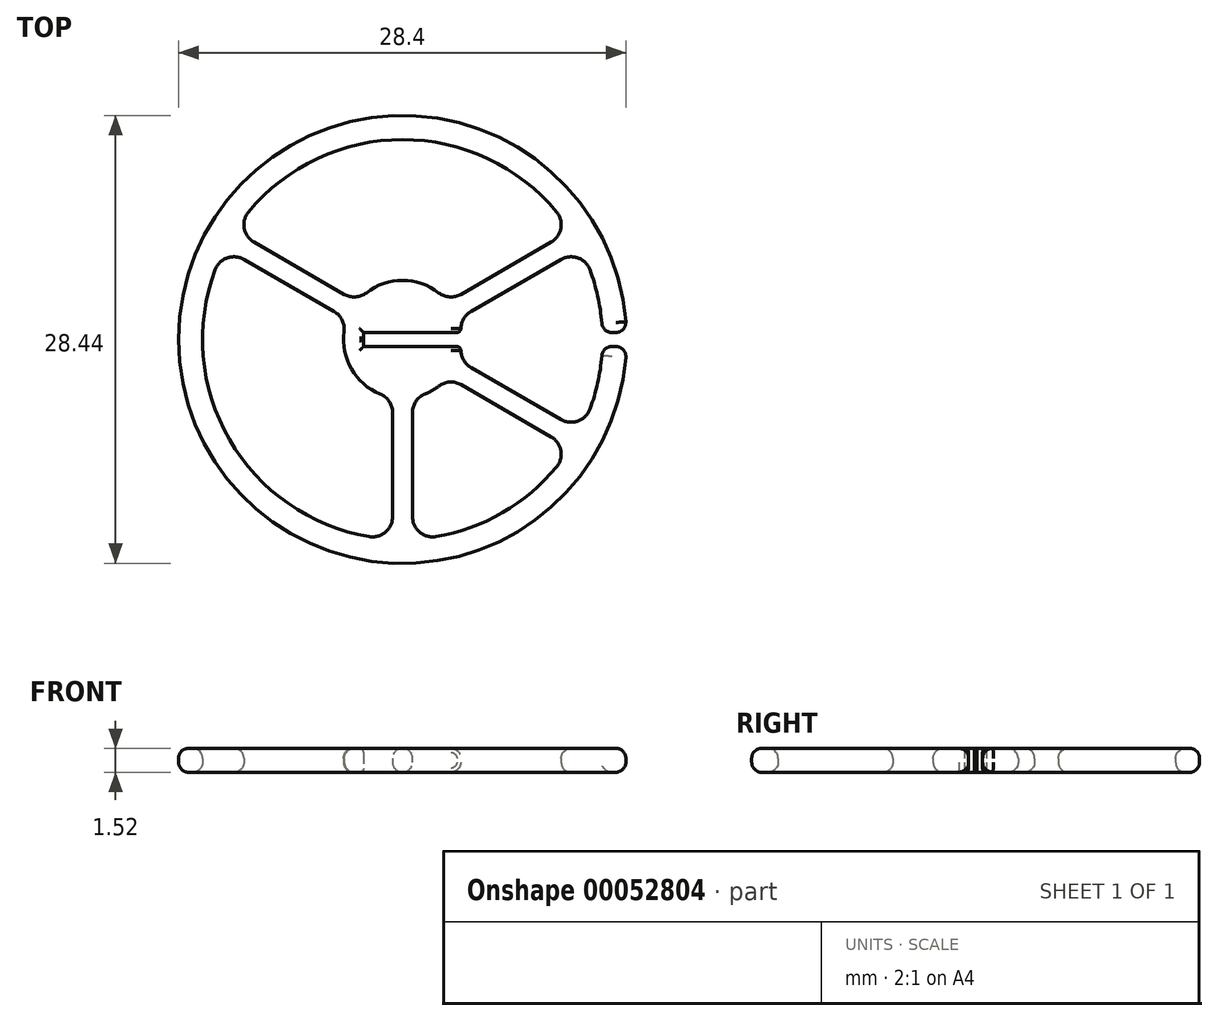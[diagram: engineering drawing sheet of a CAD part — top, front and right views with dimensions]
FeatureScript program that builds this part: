
annotation { "Feature Type Name" : "Feature", "Feature Type Description" : "" }
export const myFeature = defineFeature(function(context is Context, id is Id, definition is map)
    precondition{}
    {
        {
            var Q0;
            Q0=qCreatedBy(makeId("Top.planeOp"),FACE);
            var sketch = newSketch(context, id + "F0", { "sketchPlane" : qUnion([Q0])});
            skCircle(sketch, "E0", {"center": v(0, 0) * mm, "radius": 12.7 * mm});
            skLineSegment(sketch, "E1", {"start": v(0, 0) * mm, "end": v(11, 6.35) * mm});
            skLineSegment(sketch, "E2", {"start": v(0, 0) * mm, "end": v(0, -12.7) * mm});
            skLineSegment(sketch, "E3", {"start": v(0, 0) * mm, "end": v(-11, 6.35) * mm});
            skCircle(sketch, "E4", {"center": v(0, 0) * mm, "radius": 14.22 * mm});
            skLineSegment(sketch, "E5", {"start": v(-0.63, -12.68) * mm, "end": v(-0.64, -0.37) * mm});
            skLineSegment(sketch, "E6", {"start": v(0.63, -0.37) * mm, "end": v(0.64, -12.68) * mm});
            skLineSegment(sketch, "E7", {"start": v(0.64, -12.68) * mm, "end": v(-0.63, -12.68) * mm});
            skLineSegment(sketch, "E8", {"start": v(-11.3, 5.8) * mm, "end": v(-0.63, -0.37) * mm});
            skLineSegment(sketch, "E9", {"start": v(-0.63, -0.37) * mm, "end": v(0, 0.73) * mm});
            skLineSegment(sketch, "E10", {"start": v(0, 0.73) * mm, "end": v(-10.67, 6.9) * mm});
            skLineSegment(sketch, "E11", {"start": v(-10.67, 6.9) * mm, "end": v(-11.3, 5.8) * mm});
            skLineSegment(sketch, "E12", {"start": v(10.67, 6.9) * mm, "end": v(0, 0.73) * mm});
            skLineSegment(sketch, "E13", {"start": v(0, 0.73) * mm, "end": v(0.64, -0.37) * mm});
            skLineSegment(sketch, "E14", {"start": v(0.64, -0.37) * mm, "end": v(11.3, 5.8) * mm});
            skLineSegment(sketch, "E15", {"start": v(11.3, 5.8) * mm, "end": v(10.67, 6.9) * mm});
            skLineSegment(sketch, "E16", {"start": v(0.64, -0.37) * mm, "end": v(-0.63, -0.37) * mm});
            skCircle(sketch, "E17", {"center": v(0, 0) * mm, "radius": 3.75 * mm});
            skCircle(sketch, "E18", {"center": v(0, 0) * mm, "radius": 2.48 * mm});
            skLineSegment(sketch, "E19.bottom", {"start": v(14.9, -0.44) * mm, "end": v(-2.48, -0.44) * mm});
            skLineSegment(sketch, "E19.top", {"start": v(14.9, 0.44) * mm, "end": v(-2.48, 0.44) * mm});
            skLineSegment(sketch, "E19.left", {"start": v(14.9, -0.44) * mm, "end": v(14.9, 0.44) * mm});
            skLineSegment(sketch, "E19.right", {"start": v(-2.48, -0.44) * mm, "end": v(-2.48, 0.44) * mm});
            skLineSegment(sketch, "E20", {"start": v(10.67, -6.9) * mm, "end": v(0.14, -0.81) * mm});
            skLineSegment(sketch, "E21", {"start": v(0.14, -0.81) * mm, "end": v(0.77, 0.29) * mm});
            skLineSegment(sketch, "E22", {"start": v(0.77, 0.29) * mm, "end": v(11.3, -5.8) * mm});
            skLineSegment(sketch, "E23", {"start": v(11.3, -5.8) * mm, "end": v(10.67, -6.9) * mm});
            skLineSegment(sketch, "E24", {"start": v(0, 0) * mm, "end": v(11, -6.35) * mm});
            skSolve(sketch);
        }
        {
            var Q0;
            {var subQ0=sQuery(id+"F0.wireOp",EDGE,"E17");var subQ1=sQuery(id+"F0.wireOp",EDGE,"E3");var subQ2=makeQuery(id+"F0.imprint","INTERSECT",VERTEX,{"derivedFrom":[subQ1,subQ0]});Q0=makeQuery(id+"F0.imprint","IMPRINT",FACE,{"disambiguationData":[TD([[makeQuery(id+"F0.imprint","IMPRINT",EDGE,{"disambiguationData":[TD([[subQ2,-1.0]])],"derivedFrom":subQ1}),1.0]])]});}
            var Q1;
            {var subQ0=sQuery(id+"F0.wireOp",EDGE,"E17");var subQ1=sQuery(id+"F0.wireOp",EDGE,"E3");var subQ2=makeQuery(id+"F0.imprint","INTERSECT",VERTEX,{"derivedFrom":[subQ1,subQ0]});Q1=makeQuery(id+"F0.imprint","IMPRINT",FACE,{"disambiguationData":[TD([[makeQuery(id+"F0.imprint","IMPRINT",EDGE,{"disambiguationData":[TD([[subQ2,-1.0]])],"derivedFrom":subQ1}),-1.0]])]});}
            var Q2;
            {var subQ0=sQuery(id+"F0.wireOp",EDGE,"E18");var subQ1=sQuery(id+"F0.wireOp",EDGE,"E3");var subQ2=makeQuery(id+"F0.imprint","INTERSECT",VERTEX,{"derivedFrom":[subQ1,subQ0]});Q2=makeQuery(id+"F0.imprint","IMPRINT",FACE,{"disambiguationData":[TD([[makeQuery(id+"F0.imprint","IMPRINT",EDGE,{"disambiguationData":[TD([[subQ2,-1.0]])],"derivedFrom":subQ1}),1.0]])]});}
            var Q3;
            {var subQ0=sQuery(id+"F0.wireOp",EDGE,"E18");var subQ1=sQuery(id+"F0.wireOp",EDGE,"E3");var subQ2=makeQuery(id+"F0.imprint","INTERSECT",VERTEX,{"derivedFrom":[subQ1,subQ0]});Q3=makeQuery(id+"F0.imprint","IMPRINT",FACE,{"disambiguationData":[TD([[makeQuery(id+"F0.imprint","IMPRINT",EDGE,{"disambiguationData":[TD([[subQ2,-1.0]])],"derivedFrom":subQ1}),-1.0]])]});}
            var Q4;
            {var subQ0=sQuery(id+"F0.wireOp",EDGE,"E18");var subQ1=sQuery(id+"F0.wireOp",EDGE,"E10");var subQ2=makeQuery(id+"F0.imprint","INTERSECT",VERTEX,{"derivedFrom":[subQ1,subQ0]});Q4=makeQuery(id+"F0.imprint","IMPRINT",FACE,{"disambiguationData":[TD([[makeQuery(id+"F0.imprint","IMPRINT",EDGE,{"disambiguationData":[TD([[subQ2,-1.0]])],"derivedFrom":subQ1}),-1.0]])]});}
            var Q5;
            {var subQ0=sQuery(id+"F0.wireOp",EDGE,"E17");var subQ1=sQuery(id+"F0.wireOp",EDGE,"E5");var subQ2=makeQuery(id+"F0.imprint","INTERSECT",VERTEX,{"derivedFrom":[subQ1,subQ0]});Q5=makeQuery(id+"F0.imprint","IMPRINT",FACE,{"disambiguationData":[TD([[makeQuery(id+"F0.imprint","IMPRINT",EDGE,{"disambiguationData":[TD([[subQ2,-1.0]])],"derivedFrom":subQ1}),1.0]])]});}
            var Q6;
            {var subQ0=sQuery(id+"F0.wireOp",EDGE,"E18");var subQ1=sQuery(id+"F0.wireOp",EDGE,"E2");var subQ2=makeQuery(id+"F0.imprint","INTERSECT",VERTEX,{"derivedFrom":[subQ1,subQ0]});Q6=makeQuery(id+"F0.imprint","IMPRINT",FACE,{"disambiguationData":[TD([[makeQuery(id+"F0.imprint","IMPRINT",EDGE,{"disambiguationData":[TD([[subQ2,-1.0]])],"derivedFrom":subQ1}),-1.0]])]});}
            var Q7;
            {var subQ0=sQuery(id+"F0.wireOp",EDGE,"E18");var subQ1=sQuery(id+"F0.wireOp",EDGE,"E2");var subQ2=makeQuery(id+"F0.imprint","INTERSECT",VERTEX,{"derivedFrom":[subQ1,subQ0]});Q7=makeQuery(id+"F0.imprint","IMPRINT",FACE,{"disambiguationData":[TD([[makeQuery(id+"F0.imprint","IMPRINT",EDGE,{"disambiguationData":[TD([[subQ2,-1.0]])],"derivedFrom":subQ1}),1.0]])]});}
            var Q8;
            {var subQ0=sQuery(id+"F0.wireOp",EDGE,"E17");var subQ1=sQuery(id+"F0.wireOp",EDGE,"E2");var subQ2=makeQuery(id+"F0.imprint","INTERSECT",VERTEX,{"derivedFrom":[subQ1,subQ0]});Q8=makeQuery(id+"F0.imprint","IMPRINT",FACE,{"disambiguationData":[TD([[makeQuery(id+"F0.imprint","IMPRINT",EDGE,{"disambiguationData":[TD([[subQ2,-1.0]])],"derivedFrom":subQ1}),-1.0]])]});}
            var Q9;
            {var subQ0=sQuery(id+"F0.wireOp",EDGE,"E17");var subQ1=sQuery(id+"F0.wireOp",EDGE,"E2");var subQ2=makeQuery(id+"F0.imprint","INTERSECT",VERTEX,{"derivedFrom":[subQ1,subQ0]});Q9=makeQuery(id+"F0.imprint","IMPRINT",FACE,{"disambiguationData":[TD([[makeQuery(id+"F0.imprint","IMPRINT",EDGE,{"disambiguationData":[TD([[subQ2,-1.0]])],"derivedFrom":subQ1}),1.0]])]});}
            var Q10;
            {var subQ0=sQuery(id+"F0.wireOp",EDGE,"E18");var subQ1=sQuery(id+"F0.wireOp",EDGE,"E6");var subQ2=makeQuery(id+"F0.imprint","INTERSECT",VERTEX,{"derivedFrom":[subQ1,subQ0]});Q10=makeQuery(id+"F0.imprint","IMPRINT",FACE,{"disambiguationData":[TD([[makeQuery(id+"F0.imprint","IMPRINT",EDGE,{"disambiguationData":[TD([[subQ2,-1.0]])],"derivedFrom":subQ1}),1.0]])]});}
            var Q11;
            {var subQ0=sQuery(id+"F0.wireOp",EDGE,"E18");var subQ1=sQuery(id+"F0.wireOp",EDGE,"E1");var subQ2=makeQuery(id+"F0.imprint","INTERSECT",VERTEX,{"derivedFrom":[subQ1,subQ0]});Q11=makeQuery(id+"F0.imprint","IMPRINT",FACE,{"disambiguationData":[TD([[makeQuery(id+"F0.imprint","IMPRINT",EDGE,{"disambiguationData":[TD([[subQ2,-1.0]])],"derivedFrom":subQ1}),-1.0]])]});}
            var Q12;
            {var subQ0=sQuery(id+"F0.wireOp",EDGE,"E18");var subQ1=sQuery(id+"F0.wireOp",EDGE,"E1");var subQ2=makeQuery(id+"F0.imprint","INTERSECT",VERTEX,{"derivedFrom":[subQ1,subQ0]});Q12=makeQuery(id+"F0.imprint","IMPRINT",FACE,{"disambiguationData":[TD([[makeQuery(id+"F0.imprint","IMPRINT",EDGE,{"disambiguationData":[TD([[subQ2,-1.0]])],"derivedFrom":subQ1}),1.0]])]});}
            var Q13;
            {var subQ0=sQuery(id+"F0.wireOp",EDGE,"E17");var subQ1=sQuery(id+"F0.wireOp",EDGE,"E1");var subQ2=makeQuery(id+"F0.imprint","INTERSECT",VERTEX,{"derivedFrom":[subQ1,subQ0]});Q13=makeQuery(id+"F0.imprint","IMPRINT",FACE,{"disambiguationData":[TD([[makeQuery(id+"F0.imprint","IMPRINT",EDGE,{"disambiguationData":[TD([[subQ2,-1.0]])],"derivedFrom":subQ1}),-1.0]])]});}
            var Q14;
            {var subQ0=sQuery(id+"F0.wireOp",EDGE,"E17");var subQ1=sQuery(id+"F0.wireOp",EDGE,"E1");var subQ2=makeQuery(id+"F0.imprint","INTERSECT",VERTEX,{"derivedFrom":[subQ1,subQ0]});Q14=makeQuery(id+"F0.imprint","IMPRINT",FACE,{"disambiguationData":[TD([[makeQuery(id+"F0.imprint","IMPRINT",EDGE,{"disambiguationData":[TD([[subQ2,-1.0]])],"derivedFrom":subQ1}),1.0]])]});}
            var Q15;
            {var subQ0=sQuery(id+"F0.wireOp",EDGE,"E3");var subQ1=sQuery(id+"F0.wireOp",EDGE,"E0");var subQ2=makeQuery(id+"F0.imprint","INTERSECT",VERTEX,{"derivedFrom":[subQ1,subQ0]});Q15=makeQuery(id+"F0.imprint","IMPRINT",FACE,{"disambiguationData":[TD([[makeQuery(id+"F0.imprint","IMPRINT",EDGE,{"disambiguationData":[TD([[subQ2,1.0]])],"derivedFrom":subQ0}),1.0]])]});}
            var Q16;
            {var subQ0=sQuery(id+"F0.wireOp",EDGE,"E3");var subQ1=sQuery(id+"F0.wireOp",EDGE,"E0");var subQ2=makeQuery(id+"F0.imprint","INTERSECT",VERTEX,{"derivedFrom":[subQ1,subQ0]});Q16=makeQuery(id+"F0.imprint","IMPRINT",FACE,{"disambiguationData":[TD([[makeQuery(id+"F0.imprint","IMPRINT",EDGE,{"disambiguationData":[TD([[subQ2,1.0]])],"derivedFrom":subQ0}),-1.0]])]});}
            var Q17;
            {var subQ0=sQuery(id+"F0.wireOp",EDGE,"E1");var subQ1=sQuery(id+"F0.wireOp",EDGE,"E0");var subQ2=makeQuery(id+"F0.imprint","INTERSECT",VERTEX,{"derivedFrom":[subQ1,subQ0]});Q17=makeQuery(id+"F0.imprint","IMPRINT",FACE,{"disambiguationData":[TD([[makeQuery(id+"F0.imprint","IMPRINT",EDGE,{"disambiguationData":[TD([[subQ2,1.0]])],"derivedFrom":subQ0}),1.0]])]});}
            var Q18;
            {var subQ0=sQuery(id+"F0.wireOp",EDGE,"E1");var subQ1=sQuery(id+"F0.wireOp",EDGE,"E0");var subQ2=makeQuery(id+"F0.imprint","INTERSECT",VERTEX,{"derivedFrom":[subQ1,subQ0]});Q18=makeQuery(id+"F0.imprint","IMPRINT",FACE,{"disambiguationData":[TD([[makeQuery(id+"F0.imprint","IMPRINT",EDGE,{"disambiguationData":[TD([[subQ2,1.0]])],"derivedFrom":subQ0}),-1.0]])]});}
            var Q19;
            {var subQ0=sQuery(id+"F0.wireOp",EDGE,"E2");var subQ1=sQuery(id+"F0.wireOp",EDGE,"E0");var subQ2=makeQuery(id+"F0.imprint","INTERSECT",VERTEX,{"derivedFrom":[subQ1,subQ0]});Q19=makeQuery(id+"F0.imprint","IMPRINT",FACE,{"disambiguationData":[TD([[makeQuery(id+"F0.imprint","IMPRINT",EDGE,{"disambiguationData":[TD([[subQ2,1.0]])],"derivedFrom":subQ0}),-1.0]])]});}
            var Q20;
            {var subQ0=sQuery(id+"F0.wireOp",EDGE,"E2");var subQ1=sQuery(id+"F0.wireOp",EDGE,"E0");var subQ2=makeQuery(id+"F0.imprint","INTERSECT",VERTEX,{"derivedFrom":[subQ1,subQ0]});Q20=makeQuery(id+"F0.imprint","IMPRINT",FACE,{"disambiguationData":[TD([[makeQuery(id+"F0.imprint","IMPRINT",EDGE,{"disambiguationData":[TD([[subQ2,1.0]])],"derivedFrom":subQ0}),1.0]])]});}
            var Q21;
            {var subQ0=sQuery(id+"F0.wireOp",EDGE,"E18");var subQ1=sQuery(id+"F0.wireOp",EDGE,"E14");var subQ2=makeQuery(id+"F0.imprint","INTERSECT",VERTEX,{"derivedFrom":[subQ1,subQ0]});Q21=makeQuery(id+"F0.imprint","IMPRINT",FACE,{"disambiguationData":[TD([[makeQuery(id+"F0.imprint","IMPRINT",EDGE,{"disambiguationData":[TD([[subQ2,-1.0]])],"derivedFrom":subQ1}),-1.0]])]});}
            var Q22;
            {var subQ0=sQuery(id+"F0.wireOp",EDGE,"E18");var subQ1=sQuery(id+"F0.wireOp",EDGE,"E5");var subQ2=makeQuery(id+"F0.imprint","INTERSECT",VERTEX,{"derivedFrom":[subQ1,subQ0]});Q22=makeQuery(id+"F0.imprint","IMPRINT",FACE,{"disambiguationData":[TD([[makeQuery(id+"F0.imprint","IMPRINT",EDGE,{"disambiguationData":[TD([[subQ2,-1.0]])],"derivedFrom":subQ1}),1.0]])]});}
            var Q23;
            {var subQ0=sQuery(id+"F0.wireOp",EDGE,"E18");var subQ1=sQuery(id+"F0.wireOp",EDGE,"E8");var subQ2=makeQuery(id+"F0.imprint","INTERSECT",VERTEX,{"derivedFrom":[subQ1,subQ0]});Q23=makeQuery(id+"F0.imprint","IMPRINT",FACE,{"disambiguationData":[TD([[makeQuery(id+"F0.imprint","IMPRINT",EDGE,{"disambiguationData":[TD([[subQ2,-1.0]])],"derivedFrom":subQ1}),-1.0]])]});}
            var Q24;
            {var subQ0=sQuery(id+"F0.wireOp",EDGE,"E19.top");var subQ1=sQuery(id+"F0.wireOp",EDGE,"E3");var subQ2=makeQuery(id+"F0.imprint","INTERSECT",VERTEX,{"derivedFrom":[subQ1,subQ0]});Q24=makeQuery(id+"F0.imprint","IMPRINT",FACE,{"disambiguationData":[TD([[makeQuery(id+"F0.imprint","IMPRINT",EDGE,{"disambiguationData":[TD([[subQ2,-1.0]])],"derivedFrom":subQ1}),1.0]])]});}
            var Q25;
            {var subQ1=sQuery(id+"F0.wireOp",EDGE,"E3");var subQ7=sQuery(id+"F0.wireOp",EDGE,"E19.top");var subQ9=makeQuery(id+"F0.imprint","INTERSECT",VERTEX,{"derivedFrom":[subQ1,subQ7]});Q25=makeQuery(id+"F0.imprint","IMPRINT",FACE,{"disambiguationData":[TD([[makeQuery(id+"F0.imprint","IMPRINT",EDGE,{"disambiguationData":[TD([[subQ9,-1.0]])],"derivedFrom":subQ1}),-1.0]])]});}
            var Q26;
            {var subQ1=sQuery(id+"F0.wireOp",EDGE,"E10");var subQ3=sQuery(id+"F0.wireOp",EDGE,"E18");var subQ4=makeQuery(id+"F0.imprint","INTERSECT",VERTEX,{"derivedFrom":[subQ1,subQ3]});Q26=makeQuery(id+"F0.imprint","IMPRINT",FACE,{"disambiguationData":[TD([[makeQuery(id+"F0.imprint","IMPRINT",EDGE,{"disambiguationData":[TD([[subQ4,1.0]])],"derivedFrom":subQ3}),1.0]])]});}
            var Q27;
            {var subQ1=sQuery(id+"F0.wireOp",EDGE,"E1");var subQ7=sQuery(id+"F0.wireOp",EDGE,"E19.top");var subQ9=makeQuery(id+"F0.imprint","INTERSECT",VERTEX,{"derivedFrom":[subQ1,subQ7]});Q27=makeQuery(id+"F0.imprint","IMPRINT",FACE,{"disambiguationData":[TD([[makeQuery(id+"F0.imprint","IMPRINT",EDGE,{"disambiguationData":[TD([[subQ9,-1.0]])],"derivedFrom":subQ1}),1.0]])]});}
            var Q28;
            {var subQ1=sQuery(id+"F0.wireOp",EDGE,"E9");var subQ3=sQuery(id+"F0.wireOp",EDGE,"E19.top");var subQ4=makeQuery(id+"F0.imprint","INTERSECT",VERTEX,{"derivedFrom":[subQ1,subQ3]});Q28=makeQuery(id+"F0.imprint","IMPRINT",FACE,{"disambiguationData":[TD([[makeQuery(id+"F0.imprint","IMPRINT",EDGE,{"disambiguationData":[TD([[subQ4,1.0]])],"derivedFrom":subQ3}),-1.0]])]});}
            var Q29;
            {var subQ0=sQuery(id+"F0.wireOp",EDGE,"E19.top");var subQ1=sQuery(id+"F0.wireOp",EDGE,"E1");var subQ2=makeQuery(id+"F0.imprint","INTERSECT",VERTEX,{"derivedFrom":[subQ1,subQ0]});Q29=makeQuery(id+"F0.imprint","IMPRINT",FACE,{"disambiguationData":[TD([[makeQuery(id+"F0.imprint","IMPRINT",EDGE,{"disambiguationData":[TD([[subQ2,-1.0]])],"derivedFrom":subQ1}),-1.0]])]});}
            var Q30;
            {var subQ0=sQuery(id+"F0.wireOp",EDGE,"E19.top");var subQ1=sQuery(id+"F0.wireOp",EDGE,"E14");var subQ2=makeQuery(id+"F0.imprint","INTERSECT",VERTEX,{"derivedFrom":[subQ1,subQ0]});Q30=makeQuery(id+"F0.imprint","IMPRINT",FACE,{"disambiguationData":[TD([[makeQuery(id+"F0.imprint","IMPRINT",EDGE,{"disambiguationData":[TD([[subQ2,-1.0]])],"derivedFrom":subQ1}),-1.0]])]});}
            var Q31;
            {var subQ0=sQuery(id+"F0.wireOp",EDGE,"E19.bottom");var subQ1=sQuery(id+"F0.wireOp",EDGE,"E6");var subQ2=makeQuery(id+"F0.imprint","INTERSECT",VERTEX,{"derivedFrom":[subQ1,subQ0]});Q31=makeQuery(id+"F0.imprint","IMPRINT",FACE,{"disambiguationData":[TD([[makeQuery(id+"F0.imprint","IMPRINT",EDGE,{"disambiguationData":[TD([[subQ2,-1.0]])],"derivedFrom":subQ1}),1.0]])]});}
            var Q32;
            {var subQ0=sQuery(id+"F0.wireOp",EDGE,"E19.bottom");var subQ1=sQuery(id+"F0.wireOp",EDGE,"E2");var subQ2=makeQuery(id+"F0.imprint","INTERSECT",VERTEX,{"derivedFrom":[subQ1,subQ0]});Q32=makeQuery(id+"F0.imprint","IMPRINT",FACE,{"disambiguationData":[TD([[makeQuery(id+"F0.imprint","IMPRINT",EDGE,{"disambiguationData":[TD([[subQ2,-1.0]])],"derivedFrom":subQ1}),1.0]])]});}
            var Q33;
            {var subQ0=sQuery(id+"F0.wireOp",EDGE,"E19.bottom");var subQ1=sQuery(id+"F0.wireOp",EDGE,"E2");var subQ2=makeQuery(id+"F0.imprint","INTERSECT",VERTEX,{"derivedFrom":[subQ1,subQ0]});Q33=makeQuery(id+"F0.imprint","IMPRINT",FACE,{"disambiguationData":[TD([[makeQuery(id+"F0.imprint","IMPRINT",EDGE,{"disambiguationData":[TD([[subQ2,-1.0]])],"derivedFrom":subQ1}),-1.0]])]});}
            var Q34;
            {var subQ0=sQuery(id+"F0.wireOp",EDGE,"E19.bottom");var subQ1=sQuery(id+"F0.wireOp",EDGE,"E6");var subQ2=makeQuery(id+"F0.imprint","INTERSECT",VERTEX,{"derivedFrom":[subQ1,subQ0]});Q34=makeQuery(id+"F0.imprint","IMPRINT",FACE,{"disambiguationData":[TD([[makeQuery(id+"F0.imprint","IMPRINT",EDGE,{"disambiguationData":[TD([[subQ2,-1.0]])],"derivedFrom":subQ1}),-1.0]])]});}
            var Q35;
            {var subQ0=sQuery(id+"F0.wireOp",EDGE,"E24");var subQ1=sQuery(id+"F0.wireOp",EDGE,"E18");var subQ2=makeQuery(id+"F0.imprint","INTERSECT",VERTEX,{"derivedFrom":[subQ1,subQ0]});Q35=makeQuery(id+"F0.imprint","IMPRINT",FACE,{"disambiguationData":[TD([[makeQuery(id+"F0.imprint","IMPRINT",EDGE,{"disambiguationData":[TD([[subQ2,-1.0]])],"derivedFrom":subQ1}),1.0]])]});}
            var Q36;
            {var subQ0=sQuery(id+"F0.wireOp",EDGE,"E20");var subQ1=sQuery(id+"F0.wireOp",EDGE,"E6");var subQ2=makeQuery(id+"F0.imprint","INTERSECT",VERTEX,{"derivedFrom":[subQ1,subQ0]});Q36=makeQuery(id+"F0.imprint","IMPRINT",FACE,{"disambiguationData":[TD([[makeQuery(id+"F0.imprint","IMPRINT",EDGE,{"disambiguationData":[TD([[subQ2,-1.0]])],"derivedFrom":subQ1}),1.0]])]});}
            var Q37;
            {var subQ0=sQuery(id+"F0.wireOp",EDGE,"E20");var subQ1=sQuery(id+"F0.wireOp",EDGE,"E17");var subQ2=makeQuery(id+"F0.imprint","INTERSECT",VERTEX,{"derivedFrom":[subQ1,subQ0]});Q37=makeQuery(id+"F0.imprint","IMPRINT",FACE,{"disambiguationData":[TD([[makeQuery(id+"F0.imprint","IMPRINT",EDGE,{"disambiguationData":[TD([[subQ2,-1.0]])],"derivedFrom":subQ1}),1.0]])]});}
            var Q38;
            {var subQ0=sQuery(id+"F0.wireOp",EDGE,"E24");var subQ1=sQuery(id+"F0.wireOp",EDGE,"E17");var subQ2=makeQuery(id+"F0.imprint","INTERSECT",VERTEX,{"derivedFrom":[subQ1,subQ0]});Q38=makeQuery(id+"F0.imprint","IMPRINT",FACE,{"disambiguationData":[TD([[makeQuery(id+"F0.imprint","IMPRINT",EDGE,{"disambiguationData":[TD([[subQ2,-1.0]])],"derivedFrom":subQ1}),1.0]])]});}
            var Q39;
            {var subQ0=sQuery(id+"F0.wireOp",EDGE,"E22");var subQ1=sQuery(id+"F0.wireOp",EDGE,"E17");var subQ2=makeQuery(id+"F0.imprint","INTERSECT",VERTEX,{"derivedFrom":[subQ1,subQ0]});Q39=makeQuery(id+"F0.imprint","IMPRINT",FACE,{"disambiguationData":[TD([[makeQuery(id+"F0.imprint","IMPRINT",EDGE,{"disambiguationData":[TD([[subQ2,-1.0]])],"derivedFrom":subQ1}),1.0]])]});}
            var Q40;
            {var subQ0=sQuery(id+"F0.wireOp",EDGE,"E22");var subQ1=sQuery(id+"F0.wireOp",EDGE,"E18");var subQ2=makeQuery(id+"F0.imprint","INTERSECT",VERTEX,{"derivedFrom":[subQ1,subQ0]});Q40=makeQuery(id+"F0.imprint","IMPRINT",FACE,{"disambiguationData":[TD([[makeQuery(id+"F0.imprint","IMPRINT",EDGE,{"disambiguationData":[TD([[subQ2,-1.0]])],"derivedFrom":subQ1}),1.0]])]});}
            var Q41;
            {var subQ0=sQuery(id+"F0.wireOp",EDGE,"E20");var subQ1=sQuery(id+"F0.wireOp",EDGE,"E17");var subQ2=makeQuery(id+"F0.imprint","INTERSECT",VERTEX,{"derivedFrom":[subQ1,subQ0]});Q41=makeQuery(id+"F0.imprint","IMPRINT",FACE,{"disambiguationData":[TD([[makeQuery(id+"F0.imprint","IMPRINT",EDGE,{"disambiguationData":[TD([[subQ2,-1.0]])],"derivedFrom":subQ1}),-1.0]])]});}
            var Q42;
            {var subQ0=sQuery(id+"F0.wireOp",EDGE,"E24");var subQ1=sQuery(id+"F0.wireOp",EDGE,"E17");var subQ2=makeQuery(id+"F0.imprint","INTERSECT",VERTEX,{"derivedFrom":[subQ1,subQ0]});Q42=makeQuery(id+"F0.imprint","IMPRINT",FACE,{"disambiguationData":[TD([[makeQuery(id+"F0.imprint","IMPRINT",EDGE,{"disambiguationData":[TD([[subQ2,-1.0]])],"derivedFrom":subQ1}),-1.0]])]});}
            var Q43;
            {var subQ1=sQuery(id+"F0.wireOp",EDGE,"E0");var subQ3=sQuery(id+"F0.wireOp",EDGE,"E24");var subQ4=makeQuery(id+"F0.imprint","INTERSECT",VERTEX,{"derivedFrom":[subQ1,subQ3]});Q43=makeQuery(id+"F0.imprint","IMPRINT",FACE,{"disambiguationData":[TD([[makeQuery(id+"F0.imprint","IMPRINT",EDGE,{"disambiguationData":[TD([[subQ4,1.0]])],"derivedFrom":subQ3}),1.0]])]});}
            var Q44;
            {var subQ8=sQuery(id+"F0.wireOp",EDGE,"E19.bottom");var subQ9=sQuery(id+"F0.wireOp",EDGE,"E4");var subQ10=makeQuery(id+"F0.imprint","INTERSECT",VERTEX,{"derivedFrom":[subQ9,subQ8]});Q44=makeQuery(id+"F0.imprint","IMPRINT",FACE,{"disambiguationData":[TD([[makeQuery(id+"F0.imprint","IMPRINT",EDGE,{"disambiguationData":[TD([[subQ10,1.0]])],"derivedFrom":subQ9}),1.0]])]});}
            var Q45;
            {var subQ1=sQuery(id+"F0.wireOp",EDGE,"E0");var subQ3=sQuery(id+"F0.wireOp",EDGE,"E24");var subQ4=makeQuery(id+"F0.imprint","INTERSECT",VERTEX,{"derivedFrom":[subQ1,subQ3]});Q45=makeQuery(id+"F0.imprint","IMPRINT",FACE,{"disambiguationData":[TD([[makeQuery(id+"F0.imprint","IMPRINT",EDGE,{"disambiguationData":[TD([[subQ4,1.0]])],"derivedFrom":subQ3}),-1.0]])]});}
            extrude(context, id + "F1", {"entities" : qUnion([Q0, Q1, Q2, Q3, Q4, Q5, Q6, Q7, Q8, Q9, Q10, Q11, Q12, Q13, Q14, Q15, Q16, Q17, Q18, Q19, Q20, Q21, Q22, Q23, Q24, Q25, Q26, Q27, Q28, Q29, Q30, Q31, Q32, Q33, Q34, Q35, Q36, Q37, Q38, Q39, Q40, Q41, Q42, Q43, Q44, Q45]), "depth" : 1.52 * mm});
        }
        {
            var Q0;
            Q0=makeQuery(id+"F1.opExtrude","SWEPT_EDGE",EDGE,{"disambiguationData":[OSD([sQuery(id+"F0.wireOp",EDGE,"E0"),sQuery(id+"F0.wireOp",EDGE,"E8"),sQuery(id+"F0.wireOp",EDGE,"E11")])]});
            var Q1;
            Q1=makeQuery(id+"F1.opExtrude","SWEPT_EDGE",EDGE,{"disambiguationData":[OSD([sQuery(id+"F0.wireOp",EDGE,"E0"),sQuery(id+"F0.wireOp",EDGE,"E14"),sQuery(id+"F0.wireOp",EDGE,"E15")])]});
            var Q2;
            Q2=makeQuery(id+"F1.opExtrude","SWEPT_EDGE",EDGE,{"disambiguationData":[OSD([sQuery(id+"F0.wireOp",EDGE,"E5"),sQuery(id+"F0.wireOp",EDGE,"E17")])]});
            var Q3;
            Q3=makeQuery(id+"F1.opExtrude","SWEPT_EDGE",EDGE,{"disambiguationData":[OSD([sQuery(id+"F0.wireOp",EDGE,"E8"),sQuery(id+"F0.wireOp",EDGE,"E17")])]});
            var Q4;
            Q4=makeQuery(id+"F1.opExtrude","SWEPT_EDGE",EDGE,{"disambiguationData":[OSD([sQuery(id+"F0.wireOp",EDGE,"E0"),sQuery(id+"F0.wireOp",EDGE,"E12"),sQuery(id+"F0.wireOp",EDGE,"E15")])]});
            var Q5;
            Q5=makeQuery(id+"F1.opExtrude","SWEPT_EDGE",EDGE,{"disambiguationData":[OSD([sQuery(id+"F0.wireOp",EDGE,"E0"),sQuery(id+"F0.wireOp",EDGE,"E5"),sQuery(id+"F0.wireOp",EDGE,"E7")])]});
            var Q6;
            Q6=makeQuery(id+"F1.opExtrude","SWEPT_EDGE",EDGE,{"disambiguationData":[OSD([sQuery(id+"F0.wireOp",EDGE,"E10"),sQuery(id+"F0.wireOp",EDGE,"E17")])]});
            var Q7;
            Q7=makeQuery(id+"F1.opExtrude","SWEPT_EDGE",EDGE,{"disambiguationData":[OSD([sQuery(id+"F0.wireOp",EDGE,"E12"),sQuery(id+"F0.wireOp",EDGE,"E17")])]});
            var Q8;
            Q8=makeQuery(id+"F1.opExtrude","SWEPT_EDGE",EDGE,{"disambiguationData":[OSD([sQuery(id+"F0.wireOp",EDGE,"E0"),sQuery(id+"F0.wireOp",EDGE,"E10"),sQuery(id+"F0.wireOp",EDGE,"E11")])]});
            var Q9;
            Q9=makeQuery(id+"F1.opExtrude","SWEPT_EDGE",EDGE,{"disambiguationData":[OSD([sQuery(id+"F0.wireOp",EDGE,"E14"),sQuery(id+"F0.wireOp",EDGE,"E17")])]});
            var Q10;
            Q10=makeQuery(id+"F1.opExtrude","SWEPT_EDGE",EDGE,{"disambiguationData":[OSD([sQuery(id+"F0.wireOp",EDGE,"E6"),sQuery(id+"F0.wireOp",EDGE,"E17")])]});
            var Q11;
            Q11=makeQuery(id+"F1.opExtrude","SWEPT_EDGE",EDGE,{"disambiguationData":[OSD([sQuery(id+"F0.wireOp",EDGE,"E0"),sQuery(id+"F0.wireOp",EDGE,"E6"),sQuery(id+"F0.wireOp",EDGE,"E7")])]});
            var Q12;
            Q12=makeQuery(id+"F1.opExtrude","SWEPT_EDGE",EDGE,{"disambiguationData":[OSD([sQuery(id+"F0.wireOp",EDGE,"E0"),sQuery(id+"F0.wireOp",EDGE,"E20"),sQuery(id+"F0.wireOp",EDGE,"E23")])]});
            var Q13;
            Q13=makeQuery(id+"F1.opExtrude","SWEPT_EDGE",EDGE,{"disambiguationData":[OSD([sQuery(id+"F0.wireOp",EDGE,"E0"),sQuery(id+"F0.wireOp",EDGE,"E22"),sQuery(id+"F0.wireOp",EDGE,"E23")])]});
            var Q14;
            Q14=makeQuery(id+"F1.opExtrude","SWEPT_EDGE",EDGE,{"disambiguationData":[OSD([sQuery(id+"F0.wireOp",EDGE,"E17"),sQuery(id+"F0.wireOp",EDGE,"E22")])]});
            var Q15;
            Q15=makeQuery(id+"F1.opExtrude","SWEPT_EDGE",EDGE,{"disambiguationData":[OSD([sQuery(id+"F0.wireOp",EDGE,"E17"),sQuery(id+"F0.wireOp",EDGE,"E20")])]});
            fillet(context, id + "F2", {"entities" : qUnion([Q0, Q1, Q2, Q3, Q4, Q5, Q6, Q7, Q8, Q9, Q10, Q11, Q12, Q13, Q14, Q15]), "radius" : 1.27 * mm, "tangentPropagation" : true, "allowEdgeOverflow" : false});
        }
        {
            var Q0;
            Q0=makeQuery(id+"F1.opExtrude","CAP_EDGE",EDGE,{"disambiguationData":[OSD([sQuery(id+"F0.wireOp",EDGE,"E4")])],"isStart":false});
            var Q1;
            {var subQ0=sQuery(id+"F0.wireOp",EDGE,"E0");Q1=makeQuery(id+"F1.opExtrude","CAP_EDGE",EDGE,{"disambiguationData":[OSD([subQ0]),TDD([makeQuery(id+"F0.imprint","IMPRINT",EDGE,{"disambiguationData":[TD([[makeQuery(id+"F0.imprint","INTERSECT",VERTEX,{"derivedFrom":[subQ0,sQuery(id+"F0.wireOp",EDGE,"E5"),sQuery(id+"F0.wireOp",EDGE,"E7")]}),1.0]])],"derivedFrom":subQ0})])],"isStart":false});}
            var Q2;
            Q2=makeQuery(id+"F1.opExtrude","CAP_EDGE",EDGE,{"disambiguationData":[OSD([sQuery(id+"F0.wireOp",EDGE,"E6")])],"isStart":false});
            var Q3;
            Q3=makeQuery(id+"F1.opExtrude","CAP_EDGE",EDGE,{"disambiguationData":[OSD([sQuery(id+"F0.wireOp",EDGE,"E22")])],"isStart":false});
            var Q4;
            {var subQ0=sQuery(id+"F0.wireOp",EDGE,"E0");Q4=makeQuery(id+"F1.opExtrude","CAP_EDGE",EDGE,{"disambiguationData":[OSD([subQ0]),TDD([makeQuery(id+"F0.imprint","IMPRINT",EDGE,{"disambiguationData":[TD([[makeQuery(id+"F0.imprint","INTERSECT",VERTEX,{"derivedFrom":[subQ0,sQuery(id+"F0.wireOp",EDGE,"E19.top")]}),-1.0]])],"derivedFrom":subQ0})])],"isStart":false});}
            var Q5;
            {var subQ0=sQuery(id+"F0.wireOp",EDGE,"E0");Q5=makeQuery(id+"F1.opExtrude","CAP_EDGE",EDGE,{"disambiguationData":[OSD([subQ0]),TDD([makeQuery(id+"F0.imprint","IMPRINT",EDGE,{"disambiguationData":[TD([[makeQuery(id+"F0.imprint","INTERSECT",VERTEX,{"derivedFrom":[subQ0,sQuery(id+"F0.wireOp",EDGE,"E10"),sQuery(id+"F0.wireOp",EDGE,"E11")]}),1.0]])],"derivedFrom":subQ0})])],"isStart":false});}
            var Q6;
            {var subQ0=sQuery(id+"F0.wireOp",EDGE,"E19.top");Q6=makeQuery(id+"F1.opExtrude","CAP_EDGE",EDGE,{"disambiguationData":[OSD([subQ0]),TDD([makeQuery(id+"F0.imprint","IMPRINT",EDGE,{"disambiguationData":[TD([[makeQuery(id+"F0.imprint","INTERSECT",VERTEX,{"derivedFrom":[sQuery(id+"F0.wireOp",EDGE,"E4"),subQ0]}),-1.0]])],"derivedFrom":subQ0})])],"isStart":false});}
            var Q7;
            Q7=makeQuery(id+"F1.opExtrude","CAP_EDGE",EDGE,{"disambiguationData":[OSD([sQuery(id+"F0.wireOp",EDGE,"E8")])],"isStart":true});
            var Q8;
            Q8=makeQuery(id+"F1.opExtrude","CAP_EDGE",EDGE,{"disambiguationData":[OSD([sQuery(id+"F0.wireOp",EDGE,"E10")])],"isStart":true});
            var Q9;
            Q9=makeQuery(id+"F1.opExtrude","CAP_EDGE",EDGE,{"disambiguationData":[OSD([sQuery(id+"F0.wireOp",EDGE,"E14")])],"isStart":true});
            var Q10;
            {var subQ0=sQuery(id+"F0.wireOp",EDGE,"E0");Q10=makeQuery(id+"F1.opExtrude","CAP_EDGE",EDGE,{"disambiguationData":[OSD([subQ0]),TDD([makeQuery(id+"F0.imprint","IMPRINT",EDGE,{"disambiguationData":[TD([[makeQuery(id+"F0.imprint","INTERSECT",VERTEX,{"derivedFrom":[subQ0,sQuery(id+"F0.wireOp",EDGE,"E19.bottom")]}),1.0]])],"derivedFrom":subQ0})])],"isStart":true});}
            var Q11;
            {var subQ0=sQuery(id+"F0.wireOp",EDGE,"E20");var subQ1=sQuery(id+"F0.wireOp",EDGE,"E17");Q11=makeQuery(id+"F2.opFillet","BLEND_EDGE",EDGE,{"blendedFrom":[makeQuery(id+"F1.opExtrude","SWEPT_EDGE",EDGE,{"disambiguationData":[OSD([subQ1,subQ0])]}),makeQuery(id+"F1.opExtrude","CAP_FACE",FACE,{"disambiguationData":[OSD([sQuery(id+"F0.wireOp",EDGE,"E0"),sQuery(id+"F0.wireOp",EDGE,"E4"),sQuery(id+"F0.wireOp",EDGE,"E5"),sQuery(id+"F0.wireOp",EDGE,"E6"),sQuery(id+"F0.wireOp",EDGE,"E8"),sQuery(id+"F0.wireOp",EDGE,"E10"),sQuery(id+"F0.wireOp",EDGE,"E12"),sQuery(id+"F0.wireOp",EDGE,"E14"),subQ1,sQuery(id+"F0.wireOp",EDGE,"E18"),sQuery(id+"F0.wireOp",EDGE,"E19.bottom"),sQuery(id+"F0.wireOp",EDGE,"E19.top"),sQuery(id+"F0.wireOp",EDGE,"E19.right"),subQ0,sQuery(id+"F0.wireOp",EDGE,"E22")])],"isStart":true})],"blendedInto":[makeQuery(id+"F1.opExtrude","CAP_FACE",FACE,{"disambiguationData":[OSD([sQuery(id+"F0.wireOp",EDGE,"E0"),sQuery(id+"F0.wireOp",EDGE,"E4"),sQuery(id+"F0.wireOp",EDGE,"E5"),sQuery(id+"F0.wireOp",EDGE,"E6"),sQuery(id+"F0.wireOp",EDGE,"E8"),sQuery(id+"F0.wireOp",EDGE,"E10"),sQuery(id+"F0.wireOp",EDGE,"E12"),sQuery(id+"F0.wireOp",EDGE,"E14"),subQ1,sQuery(id+"F0.wireOp",EDGE,"E18"),sQuery(id+"F0.wireOp",EDGE,"E19.bottom"),sQuery(id+"F0.wireOp",EDGE,"E19.top"),sQuery(id+"F0.wireOp",EDGE,"E19.right"),subQ0,sQuery(id+"F0.wireOp",EDGE,"E22")])],"isStart":true})]});}
            var Q12;
            Q12=makeQuery(id+"F1.opExtrude","SWEPT_EDGE",EDGE,{"disambiguationData":[OSD([sQuery(id+"F0.wireOp",EDGE,"E4"),sQuery(id+"F0.wireOp",EDGE,"E19.top")])]});
            var Q13;
            Q13=makeQuery(id+"F1.opExtrude","SWEPT_EDGE",EDGE,{"disambiguationData":[OSD([sQuery(id+"F0.wireOp",EDGE,"E4"),sQuery(id+"F0.wireOp",EDGE,"E19.bottom")])]});
            var Q14;
            {var subQ0=sQuery(id+"F0.wireOp",EDGE,"E19.bottom");Q14=makeQuery(id+"F1.opExtrude","CAP_EDGE",EDGE,{"disambiguationData":[OSD([subQ0]),TDD([makeQuery(id+"F0.imprint","IMPRINT",EDGE,{"disambiguationData":[TD([[makeQuery(id+"F0.imprint","INTERSECT",VERTEX,{"derivedFrom":[sQuery(id+"F0.wireOp",EDGE,"E4"),subQ0]}),-1.0]])],"derivedFrom":subQ0})])],"isStart":true});}
            var Q15;
            {var subQ0=sQuery(id+"F0.wireOp",EDGE,"E19.top");Q15=makeQuery(id+"F1.opExtrude","CAP_EDGE",EDGE,{"disambiguationData":[OSD([subQ0]),TDD([makeQuery(id+"F0.imprint","IMPRINT",EDGE,{"disambiguationData":[TD([[makeQuery(id+"F0.imprint","INTERSECT",VERTEX,{"derivedFrom":[sQuery(id+"F0.wireOp",EDGE,"E4"),subQ0]}),-1.0]])],"derivedFrom":subQ0})])],"isStart":true});}
            var Q16;
            Q16=makeQuery(id+"F1.opExtrude","SWEPT_EDGE",EDGE,{"disambiguationData":[OSD([sQuery(id+"F0.wireOp",EDGE,"E0"),sQuery(id+"F0.wireOp",EDGE,"E19.top")])]});
            var Q17;
            Q17=makeQuery(id+"F1.opExtrude","SWEPT_EDGE",EDGE,{"disambiguationData":[OSD([sQuery(id+"F0.wireOp",EDGE,"E0"),sQuery(id+"F0.wireOp",EDGE,"E19.bottom")])]});
            var Q18;
            {var subQ0=sQuery(id+"F0.wireOp",EDGE,"E19.bottom");Q18=makeQuery(id+"F1.opExtrude","CAP_EDGE",EDGE,{"disambiguationData":[OSD([subQ0]),TDD([makeQuery(id+"F0.imprint","IMPRINT",EDGE,{"disambiguationData":[TD([[makeQuery(id+"F0.imprint","INTERSECT",VERTEX,{"derivedFrom":[sQuery(id+"F0.wireOp",EDGE,"E4"),subQ0]}),-1.0]])],"derivedFrom":subQ0})])],"isStart":false});}
            var Q19;
            Q19=makeQuery(id+"F1.opExtrude","CAP_EDGE",EDGE,{"disambiguationData":[OSD([sQuery(id+"F0.wireOp",EDGE,"E4")])],"isStart":true});
            fillet(context, id + "F3", {"entities" : qUnion([Q0, Q1, Q2, Q3, Q4, Q5, Q6, Q7, Q8, Q9, Q10, Q11, Q12, Q13, Q14, Q15, Q16, Q17, Q18, Q19]), "radius" : 0.64 * mm, "tangentPropagation" : true, "allowEdgeOverflow" : false});
        }
        {
            var Q0;
            {var subQ0=sQuery(id+"F0.wireOp",EDGE,"E19.top");var subQ3=makeQuery(id+"F0.imprint","INTERSECT",VERTEX,{"derivedFrom":[sQuery(id+"F0.wireOp",EDGE,"E8"),subQ0]});var subQ4=makeQuery(id+"F0.imprint","INTERSECT",VERTEX,{"derivedFrom":[sQuery(id+"F0.wireOp",EDGE,"E3"),subQ0]});var subQ5=makeQuery(id+"F0.imprint","INTERSECT",VERTEX,{"derivedFrom":[sQuery(id+"F0.wireOp",EDGE,"E9"),subQ0]});var subQ7=makeQuery(id+"F0.imprint","INTERSECT",VERTEX,{"derivedFrom":[sQuery(id+"F0.wireOp",EDGE,"E1"),subQ0]});var subQ8=makeQuery(id+"F0.imprint","INTERSECT",VERTEX,{"derivedFrom":[sQuery(id+"F0.wireOp",EDGE,"E14"),subQ0]});Q0=makeQuery(id+"F1.opExtrude","CAP_EDGE",EDGE,{"disambiguationData":[OSD([subQ0]),TDD([makeQuery(id+"F0.imprint","IMPRINT",EDGE,{"disambiguationData":[TD([[makeQuery(id+"F0.imprint","INTERSECT",VERTEX,{"derivedFrom":[sQuery(id+"F0.wireOp",EDGE,"E17"),subQ0]}),-1.0]])],"derivedFrom":subQ0}),makeQuery(id+"F0.imprint","IMPRINT",EDGE,{"disambiguationData":[TD([[subQ8,1.0]])],"derivedFrom":subQ0}),makeQuery(id+"F0.imprint","IMPRINT",EDGE,{"disambiguationData":[TD([[subQ7,1.0]])],"derivedFrom":subQ0}),makeQuery(id+"F0.imprint","IMPRINT",EDGE,{"disambiguationData":[TD([[subQ7,-1.0]])],"derivedFrom":subQ0}),makeQuery(id+"F0.imprint","IMPRINT",EDGE,{"disambiguationData":[TD([[subQ5,1.0]])],"derivedFrom":subQ0}),makeQuery(id+"F0.imprint","IMPRINT",EDGE,{"disambiguationData":[TD([[subQ4,1.0]])],"derivedFrom":subQ0}),makeQuery(id+"F0.imprint","IMPRINT",EDGE,{"disambiguationData":[TD([[subQ4,-1.0]])],"derivedFrom":subQ0}),makeQuery(id+"F0.imprint","IMPRINT",EDGE,{"disambiguationData":[TD([[subQ3,-1.0]])],"derivedFrom":subQ0}),makeQuery(id+"F0.imprint","IMPRINT",EDGE,{"disambiguationData":[TD([[makeQuery(id+"F0.imprint","INTERSECT",VERTEX,{"derivedFrom":[subQ0,sQuery(id+"F0.wireOp",EDGE,"E19.right")]}),1.0]])],"derivedFrom":subQ0})])],"isStart":false});}
            var Q1;
            {var subQ0=sQuery(id+"F0.wireOp",EDGE,"E19.right");Q1=makeQuery(id+"F1.opExtrude","CAP_EDGE",EDGE,{"disambiguationData":[OSD([subQ0]),TDD([makeQuery(id+"F0.imprint","IMPRINT",EDGE,{"disambiguationData":[TD([[makeQuery(id+"F0.imprint","INTERSECT",VERTEX,{"derivedFrom":[sQuery(id+"F0.wireOp",EDGE,"E19.top"),subQ0]}),1.0]])],"derivedFrom":subQ0})])],"isStart":false});}
            var Q2;
            {var subQ0=sQuery(id+"F0.wireOp",EDGE,"E19.right");Q2=makeQuery(id+"F1.opExtrude","CAP_EDGE",EDGE,{"disambiguationData":[OSD([subQ0]),TDD([makeQuery(id+"F0.imprint","IMPRINT",EDGE,{"disambiguationData":[TD([[makeQuery(id+"F0.imprint","INTERSECT",VERTEX,{"derivedFrom":[sQuery(id+"F0.wireOp",EDGE,"E19.bottom"),subQ0]}),-1.0]])],"derivedFrom":subQ0})])],"isStart":false});}
            var Q3;
            Q3=makeQuery(id+"F1.opExtrude","CAP_EDGE",EDGE,{"disambiguationData":[OSD([sQuery(id+"F0.wireOp",EDGE,"E18")])],"isStart":false});
            var Q4;
            {var subQ0=sQuery(id+"F0.wireOp",EDGE,"E19.bottom");var subQ1=sQuery(id+"F0.wireOp",EDGE,"E18");var subQ3=makeQuery(id+"F0.imprint","INTERSECT",VERTEX,{"derivedFrom":[sQuery(id+"F0.wireOp",EDGE,"E5"),subQ0]});var subQ4=makeQuery(id+"F0.imprint","INTERSECT",VERTEX,{"derivedFrom":[sQuery(id+"F0.wireOp",EDGE,"E2"),subQ0]});var subQ6=makeQuery(id+"F0.imprint","INTERSECT",VERTEX,{"derivedFrom":[sQuery(id+"F0.wireOp",EDGE,"E6"),subQ0]});var subQ8=makeQuery(id+"F0.imprint","INTERSECT",VERTEX,{"derivedFrom":[subQ0,sQuery(id+"F0.wireOp",EDGE,"E22")]});var subQ9=makeQuery(id+"F0.imprint","INTERSECT",VERTEX,{"disambiguationData":[OD(1.0)],"derivedFrom":[subQ1,subQ0]});Q4=makeQuery(id+"F1.opExtrude","CAP_EDGE",EDGE,{"disambiguationData":[OSD([subQ0]),TDD([makeQuery(id+"F0.imprint","IMPRINT",EDGE,{"disambiguationData":[TD([[makeQuery(id+"F0.imprint","INTERSECT",VERTEX,{"derivedFrom":[sQuery(id+"F0.wireOp",EDGE,"E17"),subQ0]}),-1.0]])],"derivedFrom":subQ0}),makeQuery(id+"F0.imprint","IMPRINT",EDGE,{"disambiguationData":[TD([[subQ9,-1.0]])],"derivedFrom":subQ0}),makeQuery(id+"F0.imprint","IMPRINT",EDGE,{"disambiguationData":[TD([[subQ8,-1.0]])],"derivedFrom":subQ0}),makeQuery(id+"F0.imprint","IMPRINT",EDGE,{"disambiguationData":[TD([[subQ6,1.0]])],"derivedFrom":subQ0}),makeQuery(id+"F0.imprint","IMPRINT",EDGE,{"disambiguationData":[TD([[subQ6,-1.0]])],"derivedFrom":subQ0}),makeQuery(id+"F0.imprint","IMPRINT",EDGE,{"disambiguationData":[TD([[subQ4,1.0]])],"derivedFrom":subQ0}),makeQuery(id+"F0.imprint","IMPRINT",EDGE,{"disambiguationData":[TD([[subQ4,-1.0]])],"derivedFrom":subQ0}),makeQuery(id+"F0.imprint","IMPRINT",EDGE,{"disambiguationData":[TD([[subQ3,-1.0]])],"derivedFrom":subQ0}),makeQuery(id+"F0.imprint","IMPRINT",EDGE,{"disambiguationData":[TD([[makeQuery(id+"F0.imprint","INTERSECT",VERTEX,{"derivedFrom":[subQ0,sQuery(id+"F0.wireOp",EDGE,"E19.right")]}),1.0]])],"derivedFrom":subQ0})])],"isStart":false});}
            var Q5;
            {var subQ0=sQuery(id+"F0.wireOp",EDGE,"E19.right");var subQ1=sQuery(id+"F0.wireOp",EDGE,"E19.top");var subQ2=sQuery(id+"F0.wireOp",EDGE,"E18");var subQ4=sQuery(id+"F0.wireOp",EDGE,"E8");var subQ5=makeQuery(id+"F0.imprint","INTERSECT",VERTEX,{"derivedFrom":[subQ4,subQ1]});var subQ6=makeQuery(id+"F0.imprint","INTERSECT",VERTEX,{"derivedFrom":[sQuery(id+"F0.wireOp",EDGE,"E3"),subQ1]});var subQ7=makeQuery(id+"F0.imprint","INTERSECT",VERTEX,{"derivedFrom":[sQuery(id+"F0.wireOp",EDGE,"E9"),subQ1]});var subQ9=makeQuery(id+"F0.imprint","INTERSECT",VERTEX,{"derivedFrom":[sQuery(id+"F0.wireOp",EDGE,"E1"),subQ1]});var subQ10=sQuery(id+"F0.wireOp",EDGE,"E14");var subQ11=makeQuery(id+"F0.imprint","INTERSECT",VERTEX,{"derivedFrom":[subQ10,subQ1]});var subQ13=sQuery(id+"F0.wireOp",EDGE,"E17");Q5=makeQuery(id+"F3.opFillet","BLEND_EDGE",EDGE,{"blendedFrom":[makeQuery(id+"F2.opFillet","BLEND_EDGE",EDGE,{"blendedFrom":[makeQuery(id+"F1.opExtrude","SWEPT_EDGE",EDGE,{"disambiguationData":[OSD([subQ10,subQ13])]}),makeQuery(id+"F1.opExtrude","CAP_FACE",FACE,{"disambiguationData":[OSD([sQuery(id+"F0.wireOp",EDGE,"E0"),sQuery(id+"F0.wireOp",EDGE,"E4"),sQuery(id+"F0.wireOp",EDGE,"E5"),sQuery(id+"F0.wireOp",EDGE,"E6"),subQ4,sQuery(id+"F0.wireOp",EDGE,"E10"),sQuery(id+"F0.wireOp",EDGE,"E12"),subQ10,subQ13,subQ2,sQuery(id+"F0.wireOp",EDGE,"E19.bottom"),subQ1,subQ0,sQuery(id+"F0.wireOp",EDGE,"E20"),sQuery(id+"F0.wireOp",EDGE,"E22")])],"isStart":false})],"blendedInto":[makeQuery(id+"F1.opExtrude","CAP_FACE",FACE,{"disambiguationData":[OSD([sQuery(id+"F0.wireOp",EDGE,"E0"),sQuery(id+"F0.wireOp",EDGE,"E4"),sQuery(id+"F0.wireOp",EDGE,"E5"),sQuery(id+"F0.wireOp",EDGE,"E6"),subQ4,sQuery(id+"F0.wireOp",EDGE,"E10"),sQuery(id+"F0.wireOp",EDGE,"E12"),subQ10,subQ13,subQ2,sQuery(id+"F0.wireOp",EDGE,"E19.bottom"),subQ1,subQ0,sQuery(id+"F0.wireOp",EDGE,"E20"),sQuery(id+"F0.wireOp",EDGE,"E22")])],"isStart":false})]}),makeQuery(id+"F1.opExtrude","SWEPT_FACE",FACE,{"disambiguationData":[OSD([subQ1]),TDD([makeQuery(id+"F0.imprint","IMPRINT",EDGE,{"disambiguationData":[TD([[makeQuery(id+"F0.imprint","INTERSECT",VERTEX,{"derivedFrom":[subQ13,subQ1]}),-1.0]])],"derivedFrom":subQ1}),makeQuery(id+"F0.imprint","IMPRINT",EDGE,{"disambiguationData":[TD([[subQ11,1.0]])],"derivedFrom":subQ1}),makeQuery(id+"F0.imprint","IMPRINT",EDGE,{"disambiguationData":[TD([[subQ9,1.0]])],"derivedFrom":subQ1}),makeQuery(id+"F0.imprint","IMPRINT",EDGE,{"disambiguationData":[TD([[subQ9,-1.0]])],"derivedFrom":subQ1}),makeQuery(id+"F0.imprint","IMPRINT",EDGE,{"disambiguationData":[TD([[subQ7,1.0]])],"derivedFrom":subQ1}),makeQuery(id+"F0.imprint","IMPRINT",EDGE,{"disambiguationData":[TD([[subQ6,1.0]])],"derivedFrom":subQ1}),makeQuery(id+"F0.imprint","IMPRINT",EDGE,{"disambiguationData":[TD([[subQ6,-1.0]])],"derivedFrom":subQ1}),makeQuery(id+"F0.imprint","IMPRINT",EDGE,{"disambiguationData":[TD([[subQ5,-1.0]])],"derivedFrom":subQ1}),makeQuery(id+"F0.imprint","IMPRINT",EDGE,{"disambiguationData":[TD([[makeQuery(id+"F0.imprint","INTERSECT",VERTEX,{"derivedFrom":[subQ1,subQ0]}),1.0]])],"derivedFrom":subQ1})])]})],"blendedInto":[makeQuery(id+"F1.opExtrude","SWEPT_FACE",FACE,{"disambiguationData":[OSD([subQ1]),TDD([makeQuery(id+"F0.imprint","IMPRINT",EDGE,{"disambiguationData":[TD([[makeQuery(id+"F0.imprint","INTERSECT",VERTEX,{"derivedFrom":[subQ13,subQ1]}),-1.0]])],"derivedFrom":subQ1}),makeQuery(id+"F0.imprint","IMPRINT",EDGE,{"disambiguationData":[TD([[subQ11,1.0]])],"derivedFrom":subQ1}),makeQuery(id+"F0.imprint","IMPRINT",EDGE,{"disambiguationData":[TD([[subQ9,1.0]])],"derivedFrom":subQ1}),makeQuery(id+"F0.imprint","IMPRINT",EDGE,{"disambiguationData":[TD([[subQ9,-1.0]])],"derivedFrom":subQ1}),makeQuery(id+"F0.imprint","IMPRINT",EDGE,{"disambiguationData":[TD([[subQ7,1.0]])],"derivedFrom":subQ1}),makeQuery(id+"F0.imprint","IMPRINT",EDGE,{"disambiguationData":[TD([[subQ6,1.0]])],"derivedFrom":subQ1}),makeQuery(id+"F0.imprint","IMPRINT",EDGE,{"disambiguationData":[TD([[subQ6,-1.0]])],"derivedFrom":subQ1}),makeQuery(id+"F0.imprint","IMPRINT",EDGE,{"disambiguationData":[TD([[subQ5,-1.0]])],"derivedFrom":subQ1}),makeQuery(id+"F0.imprint","IMPRINT",EDGE,{"disambiguationData":[TD([[makeQuery(id+"F0.imprint","INTERSECT",VERTEX,{"derivedFrom":[subQ1,subQ0]}),1.0]])],"derivedFrom":subQ1})])]})]});}
            var Q6;
            {var subQ0=sQuery(id+"F0.wireOp",EDGE,"E19.right");var subQ1=sQuery(id+"F0.wireOp",EDGE,"E19.bottom");var subQ2=sQuery(id+"F0.wireOp",EDGE,"E18");var subQ4=sQuery(id+"F0.wireOp",EDGE,"E5");var subQ5=makeQuery(id+"F0.imprint","INTERSECT",VERTEX,{"derivedFrom":[subQ4,subQ1]});var subQ6=makeQuery(id+"F0.imprint","INTERSECT",VERTEX,{"derivedFrom":[sQuery(id+"F0.wireOp",EDGE,"E2"),subQ1]});var subQ8=sQuery(id+"F0.wireOp",EDGE,"E6");var subQ9=makeQuery(id+"F0.imprint","INTERSECT",VERTEX,{"derivedFrom":[subQ8,subQ1]});var subQ11=sQuery(id+"F0.wireOp",EDGE,"E22");var subQ12=makeQuery(id+"F0.imprint","INTERSECT",VERTEX,{"derivedFrom":[subQ1,subQ11]});var subQ13=makeQuery(id+"F0.imprint","INTERSECT",VERTEX,{"disambiguationData":[OD(1.0)],"derivedFrom":[subQ2,subQ1]});var subQ14=sQuery(id+"F0.wireOp",EDGE,"E17");Q6=makeQuery(id+"F3.opFillet","BLEND_EDGE",EDGE,{"blendedFrom":[makeQuery(id+"F2.opFillet","BLEND_EDGE",EDGE,{"blendedFrom":[makeQuery(id+"F1.opExtrude","SWEPT_EDGE",EDGE,{"disambiguationData":[OSD([subQ14,subQ11])]}),makeQuery(id+"F1.opExtrude","CAP_FACE",FACE,{"disambiguationData":[OSD([sQuery(id+"F0.wireOp",EDGE,"E0"),sQuery(id+"F0.wireOp",EDGE,"E4"),subQ4,subQ8,sQuery(id+"F0.wireOp",EDGE,"E8"),sQuery(id+"F0.wireOp",EDGE,"E10"),sQuery(id+"F0.wireOp",EDGE,"E12"),sQuery(id+"F0.wireOp",EDGE,"E14"),subQ14,subQ2,subQ1,sQuery(id+"F0.wireOp",EDGE,"E19.top"),subQ0,sQuery(id+"F0.wireOp",EDGE,"E20"),subQ11])],"isStart":false})],"blendedInto":[makeQuery(id+"F1.opExtrude","CAP_FACE",FACE,{"disambiguationData":[OSD([sQuery(id+"F0.wireOp",EDGE,"E0"),sQuery(id+"F0.wireOp",EDGE,"E4"),subQ4,subQ8,sQuery(id+"F0.wireOp",EDGE,"E8"),sQuery(id+"F0.wireOp",EDGE,"E10"),sQuery(id+"F0.wireOp",EDGE,"E12"),sQuery(id+"F0.wireOp",EDGE,"E14"),subQ14,subQ2,subQ1,sQuery(id+"F0.wireOp",EDGE,"E19.top"),subQ0,sQuery(id+"F0.wireOp",EDGE,"E20"),subQ11])],"isStart":false})]}),makeQuery(id+"F1.opExtrude","SWEPT_FACE",FACE,{"disambiguationData":[OSD([subQ1]),TDD([makeQuery(id+"F0.imprint","IMPRINT",EDGE,{"disambiguationData":[TD([[makeQuery(id+"F0.imprint","INTERSECT",VERTEX,{"derivedFrom":[subQ14,subQ1]}),-1.0]])],"derivedFrom":subQ1}),makeQuery(id+"F0.imprint","IMPRINT",EDGE,{"disambiguationData":[TD([[subQ13,-1.0]])],"derivedFrom":subQ1}),makeQuery(id+"F0.imprint","IMPRINT",EDGE,{"disambiguationData":[TD([[subQ12,-1.0]])],"derivedFrom":subQ1}),makeQuery(id+"F0.imprint","IMPRINT",EDGE,{"disambiguationData":[TD([[subQ9,1.0]])],"derivedFrom":subQ1}),makeQuery(id+"F0.imprint","IMPRINT",EDGE,{"disambiguationData":[TD([[subQ9,-1.0]])],"derivedFrom":subQ1}),makeQuery(id+"F0.imprint","IMPRINT",EDGE,{"disambiguationData":[TD([[subQ6,1.0]])],"derivedFrom":subQ1}),makeQuery(id+"F0.imprint","IMPRINT",EDGE,{"disambiguationData":[TD([[subQ6,-1.0]])],"derivedFrom":subQ1}),makeQuery(id+"F0.imprint","IMPRINT",EDGE,{"disambiguationData":[TD([[subQ5,-1.0]])],"derivedFrom":subQ1}),makeQuery(id+"F0.imprint","IMPRINT",EDGE,{"disambiguationData":[TD([[makeQuery(id+"F0.imprint","INTERSECT",VERTEX,{"derivedFrom":[subQ1,subQ0]}),1.0]])],"derivedFrom":subQ1})])]})],"blendedInto":[makeQuery(id+"F1.opExtrude","SWEPT_FACE",FACE,{"disambiguationData":[OSD([subQ1]),TDD([makeQuery(id+"F0.imprint","IMPRINT",EDGE,{"disambiguationData":[TD([[makeQuery(id+"F0.imprint","INTERSECT",VERTEX,{"derivedFrom":[subQ14,subQ1]}),-1.0]])],"derivedFrom":subQ1}),makeQuery(id+"F0.imprint","IMPRINT",EDGE,{"disambiguationData":[TD([[subQ13,-1.0]])],"derivedFrom":subQ1}),makeQuery(id+"F0.imprint","IMPRINT",EDGE,{"disambiguationData":[TD([[subQ12,-1.0]])],"derivedFrom":subQ1}),makeQuery(id+"F0.imprint","IMPRINT",EDGE,{"disambiguationData":[TD([[subQ9,1.0]])],"derivedFrom":subQ1}),makeQuery(id+"F0.imprint","IMPRINT",EDGE,{"disambiguationData":[TD([[subQ9,-1.0]])],"derivedFrom":subQ1}),makeQuery(id+"F0.imprint","IMPRINT",EDGE,{"disambiguationData":[TD([[subQ6,1.0]])],"derivedFrom":subQ1}),makeQuery(id+"F0.imprint","IMPRINT",EDGE,{"disambiguationData":[TD([[subQ6,-1.0]])],"derivedFrom":subQ1}),makeQuery(id+"F0.imprint","IMPRINT",EDGE,{"disambiguationData":[TD([[subQ5,-1.0]])],"derivedFrom":subQ1}),makeQuery(id+"F0.imprint","IMPRINT",EDGE,{"disambiguationData":[TD([[makeQuery(id+"F0.imprint","INTERSECT",VERTEX,{"derivedFrom":[subQ1,subQ0]}),1.0]])],"derivedFrom":subQ1})])]})]});}
            var Q7;
            {var subQ0=sQuery(id+"F0.wireOp",EDGE,"E19.right");Q7=makeQuery(id+"F1.opExtrude","CAP_EDGE",EDGE,{"disambiguationData":[OSD([subQ0]),TDD([makeQuery(id+"F0.imprint","IMPRINT",EDGE,{"disambiguationData":[TD([[makeQuery(id+"F0.imprint","INTERSECT",VERTEX,{"derivedFrom":[sQuery(id+"F0.wireOp",EDGE,"E19.top"),subQ0]}),1.0]])],"derivedFrom":subQ0})])],"isStart":true});}
            var Q8;
            {var subQ0=sQuery(id+"F0.wireOp",EDGE,"E19.top");var subQ3=makeQuery(id+"F0.imprint","INTERSECT",VERTEX,{"derivedFrom":[sQuery(id+"F0.wireOp",EDGE,"E8"),subQ0]});var subQ4=makeQuery(id+"F0.imprint","INTERSECT",VERTEX,{"derivedFrom":[sQuery(id+"F0.wireOp",EDGE,"E3"),subQ0]});var subQ5=makeQuery(id+"F0.imprint","INTERSECT",VERTEX,{"derivedFrom":[sQuery(id+"F0.wireOp",EDGE,"E9"),subQ0]});var subQ7=makeQuery(id+"F0.imprint","INTERSECT",VERTEX,{"derivedFrom":[sQuery(id+"F0.wireOp",EDGE,"E1"),subQ0]});var subQ8=makeQuery(id+"F0.imprint","INTERSECT",VERTEX,{"derivedFrom":[sQuery(id+"F0.wireOp",EDGE,"E14"),subQ0]});Q8=makeQuery(id+"F1.opExtrude","CAP_EDGE",EDGE,{"disambiguationData":[OSD([subQ0]),TDD([makeQuery(id+"F0.imprint","IMPRINT",EDGE,{"disambiguationData":[TD([[makeQuery(id+"F0.imprint","INTERSECT",VERTEX,{"derivedFrom":[sQuery(id+"F0.wireOp",EDGE,"E17"),subQ0]}),-1.0]])],"derivedFrom":subQ0}),makeQuery(id+"F0.imprint","IMPRINT",EDGE,{"disambiguationData":[TD([[subQ8,1.0]])],"derivedFrom":subQ0}),makeQuery(id+"F0.imprint","IMPRINT",EDGE,{"disambiguationData":[TD([[subQ7,1.0]])],"derivedFrom":subQ0}),makeQuery(id+"F0.imprint","IMPRINT",EDGE,{"disambiguationData":[TD([[subQ7,-1.0]])],"derivedFrom":subQ0}),makeQuery(id+"F0.imprint","IMPRINT",EDGE,{"disambiguationData":[TD([[subQ5,1.0]])],"derivedFrom":subQ0}),makeQuery(id+"F0.imprint","IMPRINT",EDGE,{"disambiguationData":[TD([[subQ4,1.0]])],"derivedFrom":subQ0}),makeQuery(id+"F0.imprint","IMPRINT",EDGE,{"disambiguationData":[TD([[subQ4,-1.0]])],"derivedFrom":subQ0}),makeQuery(id+"F0.imprint","IMPRINT",EDGE,{"disambiguationData":[TD([[subQ3,-1.0]])],"derivedFrom":subQ0}),makeQuery(id+"F0.imprint","IMPRINT",EDGE,{"disambiguationData":[TD([[makeQuery(id+"F0.imprint","INTERSECT",VERTEX,{"derivedFrom":[subQ0,sQuery(id+"F0.wireOp",EDGE,"E19.right")]}),1.0]])],"derivedFrom":subQ0})])],"isStart":true});}
            var Q9;
            {var subQ0=sQuery(id+"F0.wireOp",EDGE,"E19.bottom");var subQ1=sQuery(id+"F0.wireOp",EDGE,"E18");var subQ3=makeQuery(id+"F0.imprint","INTERSECT",VERTEX,{"derivedFrom":[sQuery(id+"F0.wireOp",EDGE,"E5"),subQ0]});var subQ4=makeQuery(id+"F0.imprint","INTERSECT",VERTEX,{"derivedFrom":[sQuery(id+"F0.wireOp",EDGE,"E2"),subQ0]});var subQ6=makeQuery(id+"F0.imprint","INTERSECT",VERTEX,{"derivedFrom":[sQuery(id+"F0.wireOp",EDGE,"E6"),subQ0]});var subQ8=makeQuery(id+"F0.imprint","INTERSECT",VERTEX,{"derivedFrom":[subQ0,sQuery(id+"F0.wireOp",EDGE,"E22")]});var subQ9=makeQuery(id+"F0.imprint","INTERSECT",VERTEX,{"disambiguationData":[OD(1.0)],"derivedFrom":[subQ1,subQ0]});Q9=makeQuery(id+"F1.opExtrude","CAP_EDGE",EDGE,{"disambiguationData":[OSD([subQ0]),TDD([makeQuery(id+"F0.imprint","IMPRINT",EDGE,{"disambiguationData":[TD([[makeQuery(id+"F0.imprint","INTERSECT",VERTEX,{"derivedFrom":[sQuery(id+"F0.wireOp",EDGE,"E17"),subQ0]}),-1.0]])],"derivedFrom":subQ0}),makeQuery(id+"F0.imprint","IMPRINT",EDGE,{"disambiguationData":[TD([[subQ9,-1.0]])],"derivedFrom":subQ0}),makeQuery(id+"F0.imprint","IMPRINT",EDGE,{"disambiguationData":[TD([[subQ8,-1.0]])],"derivedFrom":subQ0}),makeQuery(id+"F0.imprint","IMPRINT",EDGE,{"disambiguationData":[TD([[subQ6,1.0]])],"derivedFrom":subQ0}),makeQuery(id+"F0.imprint","IMPRINT",EDGE,{"disambiguationData":[TD([[subQ6,-1.0]])],"derivedFrom":subQ0}),makeQuery(id+"F0.imprint","IMPRINT",EDGE,{"disambiguationData":[TD([[subQ4,1.0]])],"derivedFrom":subQ0}),makeQuery(id+"F0.imprint","IMPRINT",EDGE,{"disambiguationData":[TD([[subQ4,-1.0]])],"derivedFrom":subQ0}),makeQuery(id+"F0.imprint","IMPRINT",EDGE,{"disambiguationData":[TD([[subQ3,-1.0]])],"derivedFrom":subQ0}),makeQuery(id+"F0.imprint","IMPRINT",EDGE,{"disambiguationData":[TD([[makeQuery(id+"F0.imprint","INTERSECT",VERTEX,{"derivedFrom":[subQ0,sQuery(id+"F0.wireOp",EDGE,"E19.right")]}),1.0]])],"derivedFrom":subQ0})])],"isStart":true});}
            var Q10;
            {var subQ0=sQuery(id+"F0.wireOp",EDGE,"E19.right");var subQ1=sQuery(id+"F0.wireOp",EDGE,"E19.bottom");var subQ2=sQuery(id+"F0.wireOp",EDGE,"E18");var subQ4=sQuery(id+"F0.wireOp",EDGE,"E5");var subQ5=makeQuery(id+"F0.imprint","INTERSECT",VERTEX,{"derivedFrom":[subQ4,subQ1]});var subQ6=makeQuery(id+"F0.imprint","INTERSECT",VERTEX,{"derivedFrom":[sQuery(id+"F0.wireOp",EDGE,"E2"),subQ1]});var subQ8=sQuery(id+"F0.wireOp",EDGE,"E6");var subQ9=makeQuery(id+"F0.imprint","INTERSECT",VERTEX,{"derivedFrom":[subQ8,subQ1]});var subQ11=sQuery(id+"F0.wireOp",EDGE,"E22");var subQ12=makeQuery(id+"F0.imprint","INTERSECT",VERTEX,{"derivedFrom":[subQ1,subQ11]});var subQ13=makeQuery(id+"F0.imprint","INTERSECT",VERTEX,{"disambiguationData":[OD(1.0)],"derivedFrom":[subQ2,subQ1]});var subQ14=sQuery(id+"F0.wireOp",EDGE,"E17");Q10=makeQuery(id+"F3.opFillet","BLEND_EDGE",EDGE,{"blendedFrom":[makeQuery(id+"F2.opFillet","BLEND_EDGE",EDGE,{"blendedFrom":[makeQuery(id+"F1.opExtrude","SWEPT_EDGE",EDGE,{"disambiguationData":[OSD([subQ14,subQ11])]}),makeQuery(id+"F1.opExtrude","CAP_FACE",FACE,{"disambiguationData":[OSD([sQuery(id+"F0.wireOp",EDGE,"E0"),sQuery(id+"F0.wireOp",EDGE,"E4"),subQ4,subQ8,sQuery(id+"F0.wireOp",EDGE,"E8"),sQuery(id+"F0.wireOp",EDGE,"E10"),sQuery(id+"F0.wireOp",EDGE,"E12"),sQuery(id+"F0.wireOp",EDGE,"E14"),subQ14,subQ2,subQ1,sQuery(id+"F0.wireOp",EDGE,"E19.top"),subQ0,sQuery(id+"F0.wireOp",EDGE,"E20"),subQ11])],"isStart":true})],"blendedInto":[makeQuery(id+"F1.opExtrude","CAP_FACE",FACE,{"disambiguationData":[OSD([sQuery(id+"F0.wireOp",EDGE,"E0"),sQuery(id+"F0.wireOp",EDGE,"E4"),subQ4,subQ8,sQuery(id+"F0.wireOp",EDGE,"E8"),sQuery(id+"F0.wireOp",EDGE,"E10"),sQuery(id+"F0.wireOp",EDGE,"E12"),sQuery(id+"F0.wireOp",EDGE,"E14"),subQ14,subQ2,subQ1,sQuery(id+"F0.wireOp",EDGE,"E19.top"),subQ0,sQuery(id+"F0.wireOp",EDGE,"E20"),subQ11])],"isStart":true})]}),makeQuery(id+"F1.opExtrude","SWEPT_FACE",FACE,{"disambiguationData":[OSD([subQ1]),TDD([makeQuery(id+"F0.imprint","IMPRINT",EDGE,{"disambiguationData":[TD([[makeQuery(id+"F0.imprint","INTERSECT",VERTEX,{"derivedFrom":[subQ14,subQ1]}),-1.0]])],"derivedFrom":subQ1}),makeQuery(id+"F0.imprint","IMPRINT",EDGE,{"disambiguationData":[TD([[subQ13,-1.0]])],"derivedFrom":subQ1}),makeQuery(id+"F0.imprint","IMPRINT",EDGE,{"disambiguationData":[TD([[subQ12,-1.0]])],"derivedFrom":subQ1}),makeQuery(id+"F0.imprint","IMPRINT",EDGE,{"disambiguationData":[TD([[subQ9,1.0]])],"derivedFrom":subQ1}),makeQuery(id+"F0.imprint","IMPRINT",EDGE,{"disambiguationData":[TD([[subQ9,-1.0]])],"derivedFrom":subQ1}),makeQuery(id+"F0.imprint","IMPRINT",EDGE,{"disambiguationData":[TD([[subQ6,1.0]])],"derivedFrom":subQ1}),makeQuery(id+"F0.imprint","IMPRINT",EDGE,{"disambiguationData":[TD([[subQ6,-1.0]])],"derivedFrom":subQ1}),makeQuery(id+"F0.imprint","IMPRINT",EDGE,{"disambiguationData":[TD([[subQ5,-1.0]])],"derivedFrom":subQ1}),makeQuery(id+"F0.imprint","IMPRINT",EDGE,{"disambiguationData":[TD([[makeQuery(id+"F0.imprint","INTERSECT",VERTEX,{"derivedFrom":[subQ1,subQ0]}),1.0]])],"derivedFrom":subQ1})])]})],"blendedInto":[makeQuery(id+"F1.opExtrude","SWEPT_FACE",FACE,{"disambiguationData":[OSD([subQ1]),TDD([makeQuery(id+"F0.imprint","IMPRINT",EDGE,{"disambiguationData":[TD([[makeQuery(id+"F0.imprint","INTERSECT",VERTEX,{"derivedFrom":[subQ14,subQ1]}),-1.0]])],"derivedFrom":subQ1}),makeQuery(id+"F0.imprint","IMPRINT",EDGE,{"disambiguationData":[TD([[subQ13,-1.0]])],"derivedFrom":subQ1}),makeQuery(id+"F0.imprint","IMPRINT",EDGE,{"disambiguationData":[TD([[subQ12,-1.0]])],"derivedFrom":subQ1}),makeQuery(id+"F0.imprint","IMPRINT",EDGE,{"disambiguationData":[TD([[subQ9,1.0]])],"derivedFrom":subQ1}),makeQuery(id+"F0.imprint","IMPRINT",EDGE,{"disambiguationData":[TD([[subQ9,-1.0]])],"derivedFrom":subQ1}),makeQuery(id+"F0.imprint","IMPRINT",EDGE,{"disambiguationData":[TD([[subQ6,1.0]])],"derivedFrom":subQ1}),makeQuery(id+"F0.imprint","IMPRINT",EDGE,{"disambiguationData":[TD([[subQ6,-1.0]])],"derivedFrom":subQ1}),makeQuery(id+"F0.imprint","IMPRINT",EDGE,{"disambiguationData":[TD([[subQ5,-1.0]])],"derivedFrom":subQ1}),makeQuery(id+"F0.imprint","IMPRINT",EDGE,{"disambiguationData":[TD([[makeQuery(id+"F0.imprint","INTERSECT",VERTEX,{"derivedFrom":[subQ1,subQ0]}),1.0]])],"derivedFrom":subQ1})])]})]});}
            var Q11;
            {var subQ0=sQuery(id+"F0.wireOp",EDGE,"E19.right");var subQ1=sQuery(id+"F0.wireOp",EDGE,"E19.top");var subQ2=sQuery(id+"F0.wireOp",EDGE,"E18");var subQ4=sQuery(id+"F0.wireOp",EDGE,"E8");var subQ5=makeQuery(id+"F0.imprint","INTERSECT",VERTEX,{"derivedFrom":[subQ4,subQ1]});var subQ6=makeQuery(id+"F0.imprint","INTERSECT",VERTEX,{"derivedFrom":[sQuery(id+"F0.wireOp",EDGE,"E3"),subQ1]});var subQ7=makeQuery(id+"F0.imprint","INTERSECT",VERTEX,{"derivedFrom":[sQuery(id+"F0.wireOp",EDGE,"E9"),subQ1]});var subQ9=makeQuery(id+"F0.imprint","INTERSECT",VERTEX,{"derivedFrom":[sQuery(id+"F0.wireOp",EDGE,"E1"),subQ1]});var subQ10=sQuery(id+"F0.wireOp",EDGE,"E14");var subQ11=makeQuery(id+"F0.imprint","INTERSECT",VERTEX,{"derivedFrom":[subQ10,subQ1]});var subQ13=sQuery(id+"F0.wireOp",EDGE,"E17");Q11=makeQuery(id+"F3.opFillet","BLEND_EDGE",EDGE,{"blendedFrom":[makeQuery(id+"F2.opFillet","BLEND_EDGE",EDGE,{"blendedFrom":[makeQuery(id+"F1.opExtrude","SWEPT_EDGE",EDGE,{"disambiguationData":[OSD([subQ10,subQ13])]}),makeQuery(id+"F1.opExtrude","CAP_FACE",FACE,{"disambiguationData":[OSD([sQuery(id+"F0.wireOp",EDGE,"E0"),sQuery(id+"F0.wireOp",EDGE,"E4"),sQuery(id+"F0.wireOp",EDGE,"E5"),sQuery(id+"F0.wireOp",EDGE,"E6"),subQ4,sQuery(id+"F0.wireOp",EDGE,"E10"),sQuery(id+"F0.wireOp",EDGE,"E12"),subQ10,subQ13,subQ2,sQuery(id+"F0.wireOp",EDGE,"E19.bottom"),subQ1,subQ0,sQuery(id+"F0.wireOp",EDGE,"E20"),sQuery(id+"F0.wireOp",EDGE,"E22")])],"isStart":true})],"blendedInto":[makeQuery(id+"F1.opExtrude","CAP_FACE",FACE,{"disambiguationData":[OSD([sQuery(id+"F0.wireOp",EDGE,"E0"),sQuery(id+"F0.wireOp",EDGE,"E4"),sQuery(id+"F0.wireOp",EDGE,"E5"),sQuery(id+"F0.wireOp",EDGE,"E6"),subQ4,sQuery(id+"F0.wireOp",EDGE,"E10"),sQuery(id+"F0.wireOp",EDGE,"E12"),subQ10,subQ13,subQ2,sQuery(id+"F0.wireOp",EDGE,"E19.bottom"),subQ1,subQ0,sQuery(id+"F0.wireOp",EDGE,"E20"),sQuery(id+"F0.wireOp",EDGE,"E22")])],"isStart":true})]}),makeQuery(id+"F1.opExtrude","SWEPT_FACE",FACE,{"disambiguationData":[OSD([subQ1]),TDD([makeQuery(id+"F0.imprint","IMPRINT",EDGE,{"disambiguationData":[TD([[makeQuery(id+"F0.imprint","INTERSECT",VERTEX,{"derivedFrom":[subQ13,subQ1]}),-1.0]])],"derivedFrom":subQ1}),makeQuery(id+"F0.imprint","IMPRINT",EDGE,{"disambiguationData":[TD([[subQ11,1.0]])],"derivedFrom":subQ1}),makeQuery(id+"F0.imprint","IMPRINT",EDGE,{"disambiguationData":[TD([[subQ9,1.0]])],"derivedFrom":subQ1}),makeQuery(id+"F0.imprint","IMPRINT",EDGE,{"disambiguationData":[TD([[subQ9,-1.0]])],"derivedFrom":subQ1}),makeQuery(id+"F0.imprint","IMPRINT",EDGE,{"disambiguationData":[TD([[subQ7,1.0]])],"derivedFrom":subQ1}),makeQuery(id+"F0.imprint","IMPRINT",EDGE,{"disambiguationData":[TD([[subQ6,1.0]])],"derivedFrom":subQ1}),makeQuery(id+"F0.imprint","IMPRINT",EDGE,{"disambiguationData":[TD([[subQ6,-1.0]])],"derivedFrom":subQ1}),makeQuery(id+"F0.imprint","IMPRINT",EDGE,{"disambiguationData":[TD([[subQ5,-1.0]])],"derivedFrom":subQ1}),makeQuery(id+"F0.imprint","IMPRINT",EDGE,{"disambiguationData":[TD([[makeQuery(id+"F0.imprint","INTERSECT",VERTEX,{"derivedFrom":[subQ1,subQ0]}),1.0]])],"derivedFrom":subQ1})])]})],"blendedInto":[makeQuery(id+"F1.opExtrude","SWEPT_FACE",FACE,{"disambiguationData":[OSD([subQ1]),TDD([makeQuery(id+"F0.imprint","IMPRINT",EDGE,{"disambiguationData":[TD([[makeQuery(id+"F0.imprint","INTERSECT",VERTEX,{"derivedFrom":[subQ13,subQ1]}),-1.0]])],"derivedFrom":subQ1}),makeQuery(id+"F0.imprint","IMPRINT",EDGE,{"disambiguationData":[TD([[subQ11,1.0]])],"derivedFrom":subQ1}),makeQuery(id+"F0.imprint","IMPRINT",EDGE,{"disambiguationData":[TD([[subQ9,1.0]])],"derivedFrom":subQ1}),makeQuery(id+"F0.imprint","IMPRINT",EDGE,{"disambiguationData":[TD([[subQ9,-1.0]])],"derivedFrom":subQ1}),makeQuery(id+"F0.imprint","IMPRINT",EDGE,{"disambiguationData":[TD([[subQ7,1.0]])],"derivedFrom":subQ1}),makeQuery(id+"F0.imprint","IMPRINT",EDGE,{"disambiguationData":[TD([[subQ6,1.0]])],"derivedFrom":subQ1}),makeQuery(id+"F0.imprint","IMPRINT",EDGE,{"disambiguationData":[TD([[subQ6,-1.0]])],"derivedFrom":subQ1}),makeQuery(id+"F0.imprint","IMPRINT",EDGE,{"disambiguationData":[TD([[subQ5,-1.0]])],"derivedFrom":subQ1}),makeQuery(id+"F0.imprint","IMPRINT",EDGE,{"disambiguationData":[TD([[makeQuery(id+"F0.imprint","INTERSECT",VERTEX,{"derivedFrom":[subQ1,subQ0]}),1.0]])],"derivedFrom":subQ1})])]})]});}
            var Q12;
            {var subQ0=sQuery(id+"F0.wireOp",EDGE,"E19.right");Q12=makeQuery(id+"F1.opExtrude","CAP_EDGE",EDGE,{"disambiguationData":[OSD([subQ0]),TDD([makeQuery(id+"F0.imprint","IMPRINT",EDGE,{"disambiguationData":[TD([[makeQuery(id+"F0.imprint","INTERSECT",VERTEX,{"derivedFrom":[sQuery(id+"F0.wireOp",EDGE,"E19.bottom"),subQ0]}),-1.0]])],"derivedFrom":subQ0})])],"isStart":true});}
            var Q13;
            Q13=makeQuery(id+"F1.opExtrude","CAP_EDGE",EDGE,{"disambiguationData":[OSD([sQuery(id+"F0.wireOp",EDGE,"E18")])],"isStart":true});
            fillet(context, id + "F4", {"entities" : qUnion([Q0, Q1, Q2, Q3, Q4, Q5, Q6, Q7, Q8, Q9, Q10, Q11, Q12, Q13]), "radius" : 0.25 * mm, "allowEdgeOverflow" : false});
        }
    });
